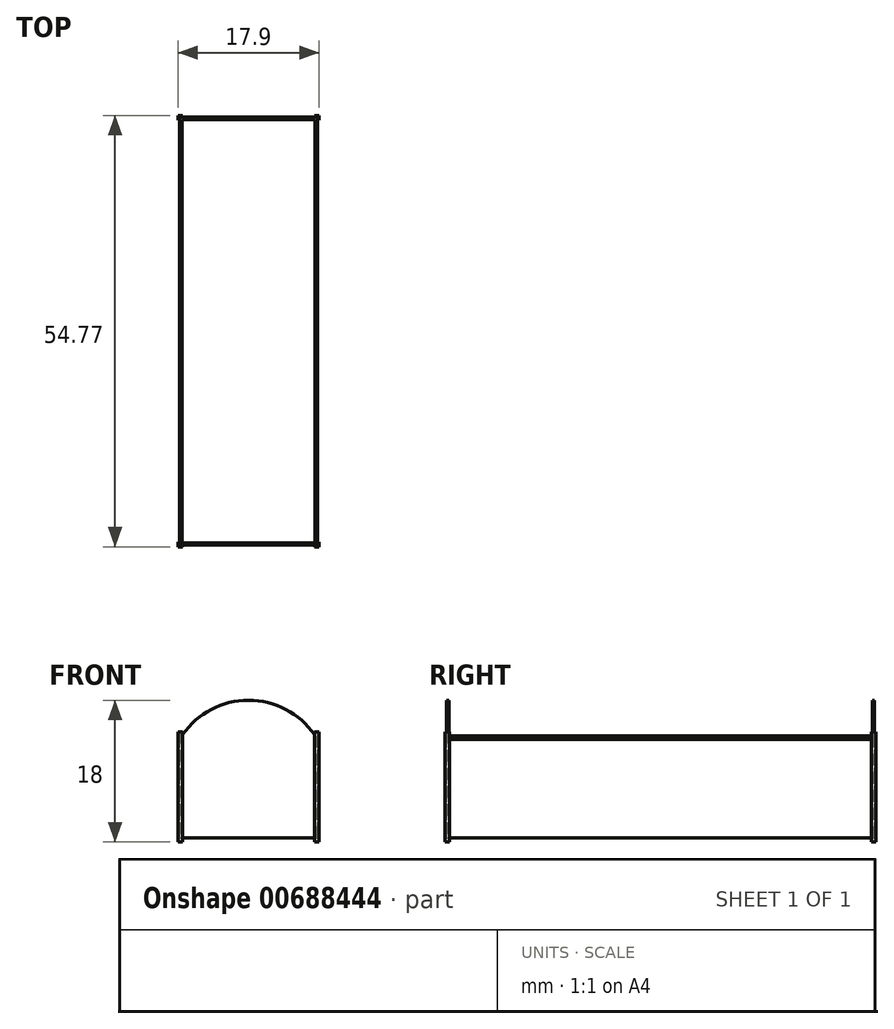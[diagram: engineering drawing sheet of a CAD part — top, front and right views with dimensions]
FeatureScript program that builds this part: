
annotation { "Feature Type Name" : "Feature", "Feature Type Description" : "" }
export const myFeature = defineFeature(function(context is Context, id is Id, definition is map)
    precondition{}
    {
        {
            var Q0;
            Q0=qCreatedBy(makeId("Front.planeOp"),FACE);
            var sketch = newSketch(context, id + "F0", { "sketchPlane" : qUnion([Q0])});
            skLineSegment(sketch, "E0.bottom", {"start": v(-8.75, 0) * mm, "end": v(8.75, 0) * mm});
            skLineSegment(sketch, "E0.top", {"start": v(-8.75, 12.5) * mm, "end": v(8.75, 12.5) * mm});
            skLineSegment(sketch, "E0.left", {"start": v(-8.75, 0) * mm, "end": v(-8.75, 12.5) * mm});
            skLineSegment(sketch, "E0.right", {"start": v(8.75, 0) * mm, "end": v(8.75, 12.5) * mm});
            skArc(sketch, "E1", {"start": v(8.75, 12.5) * mm, "mid": v(0, 17.5) * mm, "end": v(-8.75, 12.5) * mm});
            skSolve(sketch);
        }
        {
            var Q0;
            Q0 = qSketchRegion(id + "F0", true);
            extrude(context, id + "F1", {"entities" : qUnion([Q0]), "depth" : 54.38 * mm, "offsetDistance" : 25 * mm});
        }
        {
            var Q0;
            Q0=makeQuery(id+"F1.opExtrude","SWEPT_FACE",FACE,{"disambiguationData":[OSD([sQuery(id+"F0.wireOp",EDGE,"E0.bottom")])]});
            var Q1;
            Q1=makeQuery(id+"F1.opExtrude","SWEPT_FACE",FACE,{"disambiguationData":[OSD([sQuery(id+"F0.wireOp",EDGE,"E1")])]});
            shell(context, id + "F2", {"entities" : qUnion([Q0, Q1]), "thickness" : 0.3 * mm});
        }
        {
            var Q0;
            Q0=qCreatedBy(makeId("Top.planeOp"),FACE);
            var sketch = newSketch(context, id + "F3", { "sketchPlane" : qUnion([Q0])});
            skLineSegment(sketch, "E2.bottom", {"start": v(-8.35, 0.2) * mm, "end": v(-8.95, 0.2) * mm});
            skLineSegment(sketch, "E2.right", {"start": v(-8.95, 0.2) * mm, "end": v(-8.95, -0.4) * mm});
            skLineSegment(sketch, "E3.bottom", {"start": v(-8.35, 0) * mm, "end": v(-8.75, 0) * mm});
            skLineSegment(sketch, "E3.right", {"start": v(-8.75, 0) * mm, "end": v(-8.75, -0.4) * mm});
            skLineSegment(sketch, "E4", {"start": v(-8.35, 0.2) * mm, "end": v(-8.35, 0) * mm});
            skLineSegment(sketch, "E5", {"start": v(-8.75, -0.4) * mm, "end": v(-8.95, -0.4) * mm});
            skLineSegment(sketch, "E6.bottom", {"start": v(8.95, -0.4) * mm, "end": v(8.95, 0.2) * mm});
            skLineSegment(sketch, "E6.right", {"start": v(8.95, 0.2) * mm, "end": v(8.35, 0.2) * mm});
            skLineSegment(sketch, "E7.bottom", {"start": v(8.75, -0.4) * mm, "end": v(8.75, 0) * mm});
            skLineSegment(sketch, "E7.right", {"start": v(8.75, 0) * mm, "end": v(8.35, 0) * mm});
            skLineSegment(sketch, "E8", {"start": v(8.95, -0.4) * mm, "end": v(8.75, -0.4) * mm});
            skLineSegment(sketch, "E9", {"start": v(8.35, 0) * mm, "end": v(8.35, 0.2) * mm});
            skLineSegment(sketch, "E10.bottom", {"start": v(-8.95, -53.98) * mm, "end": v(-8.95, -54.57) * mm});
            skLineSegment(sketch, "E10.right", {"start": v(-8.95, -54.58) * mm, "end": v(-8.35, -54.58) * mm});
            skLineSegment(sketch, "E11.bottom", {"start": v(-8.75, -53.97) * mm, "end": v(-8.75, -54.38) * mm});
            skLineSegment(sketch, "E11.right", {"start": v(-8.75, -54.38) * mm, "end": v(-8.35, -54.38) * mm});
            skLineSegment(sketch, "E12", {"start": v(-8.95, -53.97) * mm, "end": v(-8.75, -53.97) * mm});
            skLineSegment(sketch, "E13", {"start": v(-8.35, -54.37) * mm, "end": v(-8.35, -54.57) * mm});
            skLineSegment(sketch, "E14.bottom", {"start": v(8.35, -54.58) * mm, "end": v(8.95, -54.58) * mm});
            skLineSegment(sketch, "E14.right", {"start": v(8.95, -54.58) * mm, "end": v(8.95, -53.98) * mm});
            skLineSegment(sketch, "E15.bottom", {"start": v(8.35, -54.38) * mm, "end": v(8.75, -54.38) * mm});
            skLineSegment(sketch, "E15.right", {"start": v(8.75, -54.38) * mm, "end": v(8.75, -53.98) * mm});
            skLineSegment(sketch, "E16", {"start": v(8.35, -54.58) * mm, "end": v(8.35, -54.38) * mm});
            skLineSegment(sketch, "E17", {"start": v(8.75, -53.98) * mm, "end": v(8.95, -53.98) * mm});
            skSolve(sketch);
        }
        {
            var Q0;
            Q0=makeQuery(id+"F3.imprint","IMPRINT",FACE,{"disambiguationData":[TD([[makeQuery(id+"F3.imprint","IMPRINT",EDGE,{"derivedFrom":sQuery(id+"F3.wireOp",EDGE,"E2.bottom")}),1.0]])]});
            var Q1;
            Q1=makeQuery(id+"F3.imprint","IMPRINT",FACE,{"disambiguationData":[TD([[makeQuery(id+"F3.imprint","IMPRINT",EDGE,{"derivedFrom":sQuery(id+"F3.wireOp",EDGE,"E6.bottom")}),1.0]])]});
            var Q2;
            Q2=makeQuery(id+"F3.imprint","IMPRINT",FACE,{"disambiguationData":[TD([[makeQuery(id+"F3.imprint","IMPRINT",EDGE,{"derivedFrom":sQuery(id+"F3.wireOp",EDGE,"E10.bottom")}),1.0]])]});
            var Q3;
            Q3=makeQuery(id+"F3.imprint","IMPRINT",FACE,{"disambiguationData":[TD([[makeQuery(id+"F3.imprint","IMPRINT",EDGE,{"derivedFrom":sQuery(id+"F3.wireOp",EDGE,"E14.bottom")}),1.0]])]});
            extrude(context, id + "F4", {"entities" : qUnion([Q0, Q1, Q2, Q3]), "depth" : 13.5 * mm, "offsetDistance" : 25 * mm, "hasSecondDirection" : true, "secondDirectionOppositeDirection" : true, "secondDirectionDepth" : 0.5 * mm});
        }
    });
